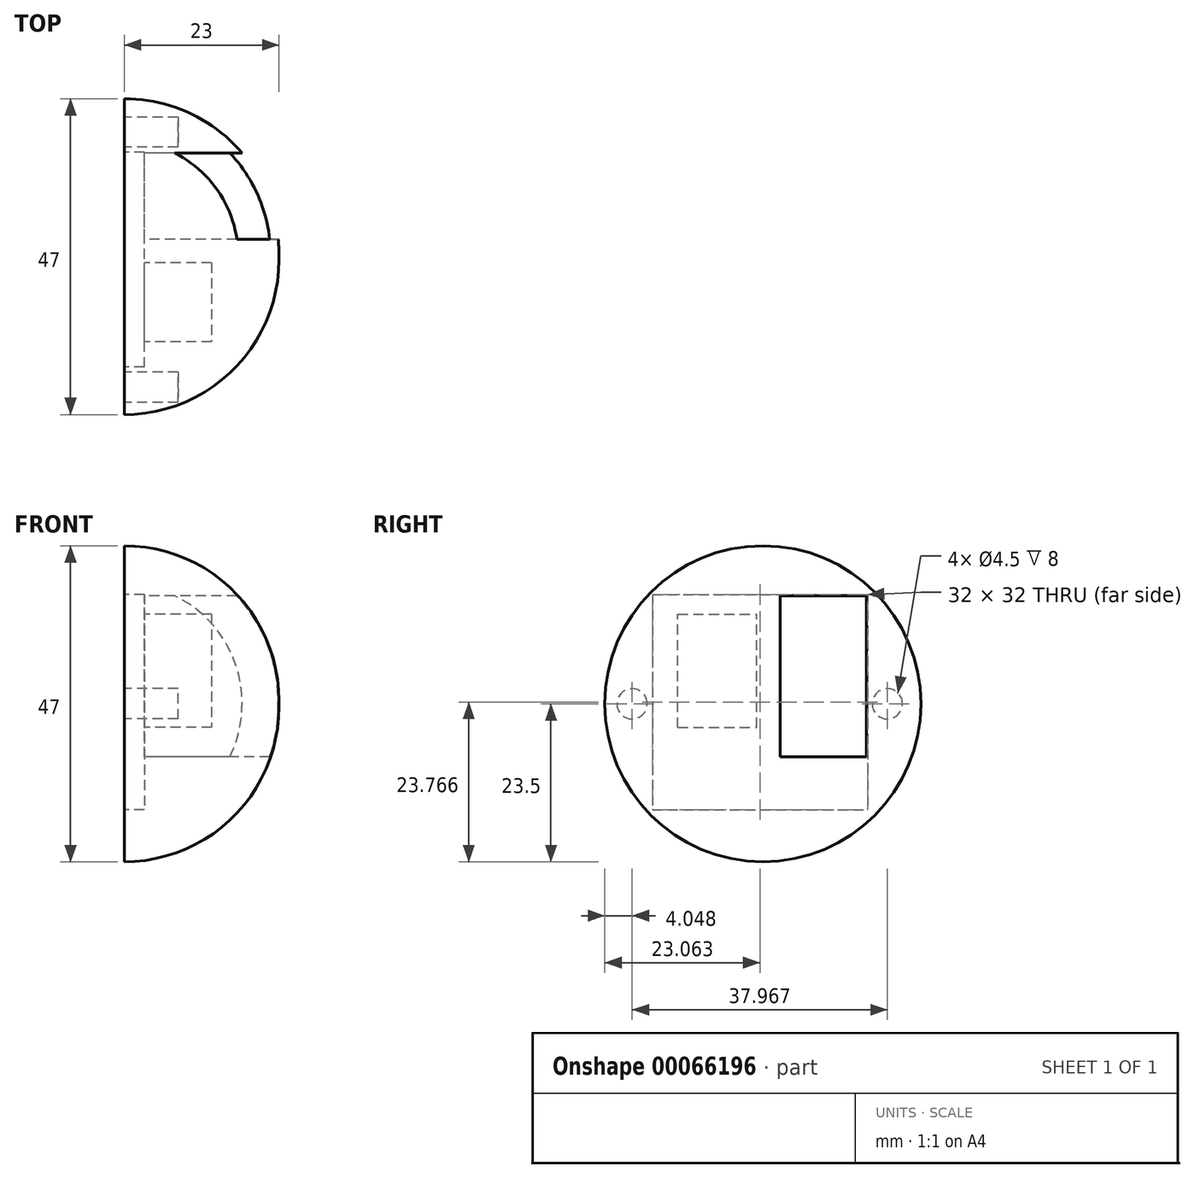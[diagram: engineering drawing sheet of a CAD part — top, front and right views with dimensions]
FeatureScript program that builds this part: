
annotation { "Feature Type Name" : "Feature", "Feature Type Description" : "" }
export const myFeature = defineFeature(function(context is Context, id is Id, definition is map)
    precondition{}
    {
        {
            var Q0;
            Q0=qCreatedBy(makeId("Right.planeOp"),FACE);
            var sketch = newSketch(context, id + "F0", { "sketchPlane" : qUnion([Q0])});
            skLineSegment(sketch, "E0.bottom", {"start": v(-16.44, 16.27) * mm, "end": v(15.56, 16.27) * mm});
            skLineSegment(sketch, "E0.top", {"start": v(-16.44, -15.73) * mm, "end": v(15.56, -15.73) * mm});
            skLineSegment(sketch, "E0.left", {"start": v(-16.44, 16.27) * mm, "end": v(-16.44, -15.73) * mm});
            skLineSegment(sketch, "E0.right", {"start": v(15.56, 16.27) * mm, "end": v(15.56, -15.73) * mm});
            skSolve(sketch);
        }
        {
            var Q0;
            Q0=qCreatedBy(makeId("Right.planeOp"),FACE);
            var sketch = newSketch(context, id + "F1", { "sketchPlane" : qUnion([Q0])});
            skCircle(sketch, "E1", {"center": v(0, 0) * mm, "radius": 23.5 * mm});
            skSolve(sketch);
        }
        {
            var Q0;
            Q0=qSketchRegion(id+"F1",true);
            extrude(context, id + "F2", {"entities" : qUnion([Q0]), "depth" : 23 * mm});
        }
        {
            var Q0;
            Q0=makeQuery(id+"F2.opExtrude","CAP_EDGE",EDGE,{"disambiguationData":[OSD([sQuery(id+"F1.wireOp",EDGE,"E1")])],"isStart":false});
            fillet(context, id + "F3", {"entities" : qUnion([Q0]), "radius" : 23 * mm, "tangentPropagation" : true, "allowEdgeOverflow" : false});
        }
        {
            var Q0;
            Q0=makeQuery(id+"F0.imprint","IMPRINT",FACE,{"disambiguationData":[TD([[makeQuery(id+"F0.imprint","IMPRINT",EDGE,{"derivedFrom":sQuery(id+"F0.wireOp",EDGE,"E0.bottom")}),-1.0]])]});
            extrude(context, id + "F4", {"entities" : qUnion([Q0]), "operationType" : NewBodyOperationType.REMOVE, "depth" : 3 * mm});
        }
        {
            var Q0;
            Q0=qCreatedBy(makeId("Right.planeOp"),FACE);
            var sketch = newSketch(context, id + "F5", { "sketchPlane" : qUnion([Q0])});
            skCircle(sketch, "E2", {"center": v(18.52, 0) * mm, "radius": 2.25 * mm});
            skCircle(sketch, "E3", {"center": v(-19.45, 0) * mm, "radius": 2.25 * mm});
            skSolve(sketch);
        }
        {
            var Q0;
            Q0 = qSketchRegion(id + "F5", true);
            extrude(context, id + "F6", {"entities" : qUnion([Q0]), "operationType" : NewBodyOperationType.REMOVE, "depth" : 8 * mm});
        }
        {
            var Q0;
            Q0=makeQuery(id+"F1.imprint","IMPRINT",FACE,{"disambiguationData":[TD([[makeQuery(id+"F1.imprint","IMPRINT",EDGE,{"derivedFrom":sQuery(id+"F1.wireOp",EDGE,"E1")}),1.0]])]});
            var sketch = newSketch(context, id + "F7", { "sketchPlane" : qUnion([Q0])});
            skLineSegment(sketch, "E4.bottom", {"start": v(15.39, 16.05) * mm, "end": v(2.59, 16.05) * mm});
            skLineSegment(sketch, "E4.top", {"start": v(15.39, -7.89) * mm, "end": v(2.59, -7.89) * mm});
            skLineSegment(sketch, "E4.left", {"start": v(15.39, 16.05) * mm, "end": v(15.39, -7.89) * mm});
            skLineSegment(sketch, "E4.right", {"start": v(2.59, 16.05) * mm, "end": v(2.59, -7.89) * mm});
            skSolve(sketch);
        }
        {
            var Q0;
            Q0=makeQuery(id+"F7.imprint","IMPRINT",FACE,{"disambiguationData":[TD([[makeQuery(id+"F7.imprint","IMPRINT",EDGE,{"derivedFrom":sQuery(id+"F7.wireOp",EDGE,"E4.bottom")}),1.0]])]});
            extrude(context, id + "F8", {"entities" : qUnion([Q0]), "operationType" : NewBodyOperationType.REMOVE, "endBound" : BoundingType.THROUGH_ALL, "depth" : 5.26 * mm});
        }
        {
            var Q0;
            Q0=qCreatedBy(makeId("Right.planeOp"),FACE);
            var sketch = newSketch(context, id + "F9", { "sketchPlane" : qUnion([Q0])});
            skLineSegment(sketch, "E5.bottom", {"start": v(-0.92, 13.31) * mm, "end": v(-12.64, 13.31) * mm});
            skLineSegment(sketch, "E5.top", {"start": v(-0.92, -3.52) * mm, "end": v(-12.64, -3.52) * mm});
            skLineSegment(sketch, "E5.left", {"start": v(-0.92, 13.31) * mm, "end": v(-0.92, -3.52) * mm});
            skLineSegment(sketch, "E5.right", {"start": v(-12.64, 13.31) * mm, "end": v(-12.64, -3.52) * mm});
            skSolve(sketch);
        }
        {
            var Q0;
            Q0 = qSketchRegion(id + "F9", true);
            extrude(context, id + "F10", {"entities" : qUnion([Q0]), "operationType" : NewBodyOperationType.REMOVE, "depth" : 13 * mm});
        }
    });
